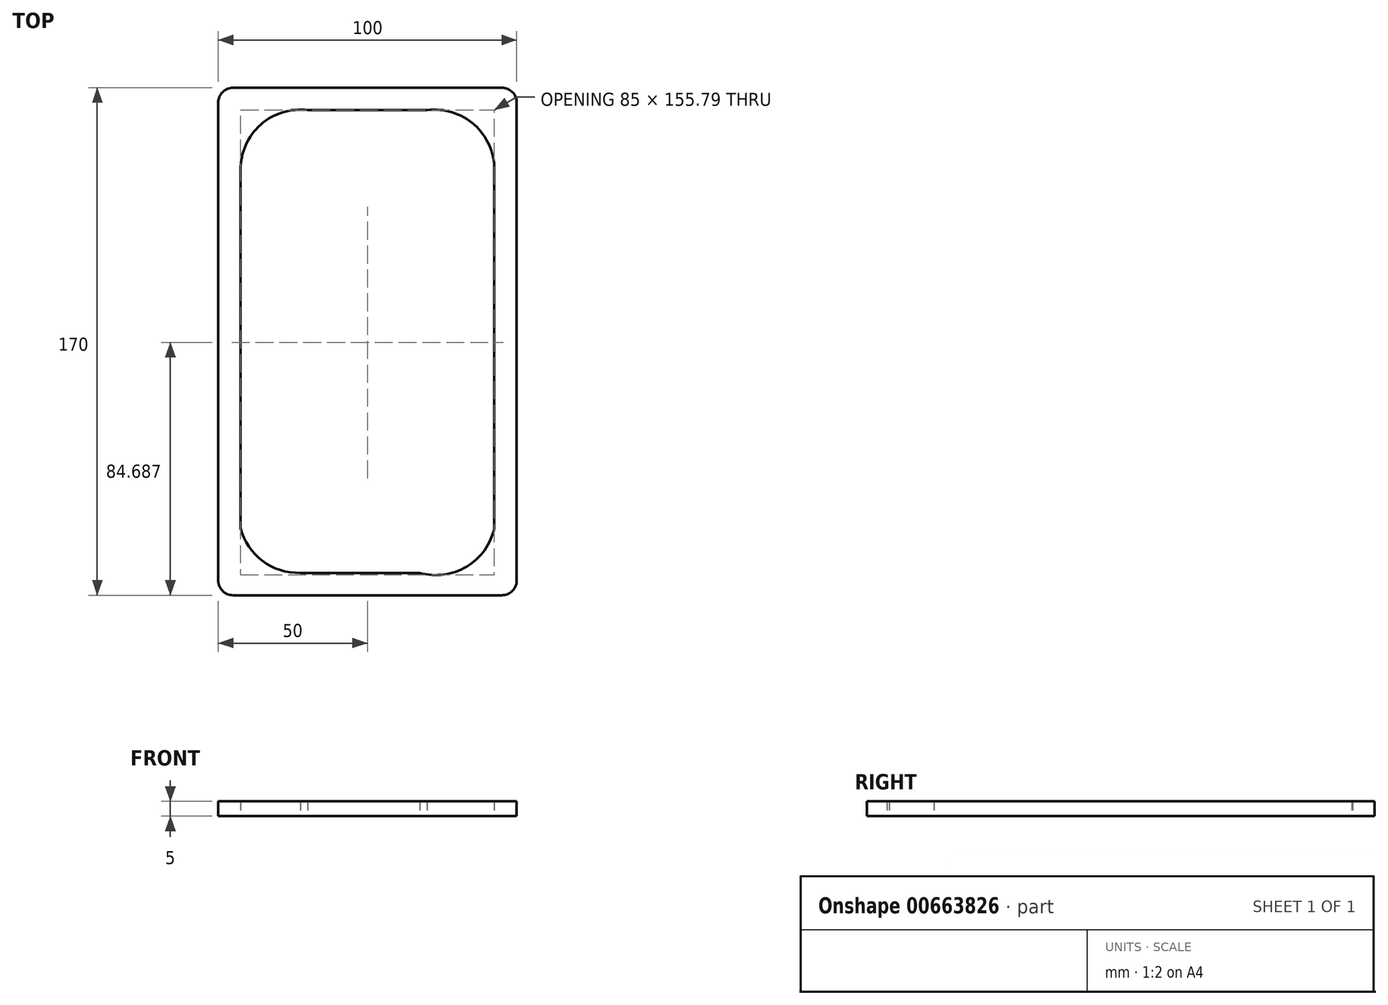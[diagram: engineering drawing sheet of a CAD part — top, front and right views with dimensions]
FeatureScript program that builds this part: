
annotation { "Feature Type Name" : "Feature", "Feature Type Description" : "" }
export const myFeature = defineFeature(function(context is Context, id is Id, definition is map)
    precondition{}
    {
        {
            var Q0;
            Q0=qCreatedBy(makeId("Top.planeOp"),FACE);
            var sketch = newSketch(context, id + "F0", { "sketchPlane" : qUnion([Q0])});
            skLineSegment(sketch, "E0.bottom", {"start": v(-45, -85) * mm, "end": v(45, -85) * mm});
            skLineSegment(sketch, "E0.top", {"start": v(-45, 85) * mm, "end": v(45, 85) * mm});
            skLineSegment(sketch, "E0.left", {"start": v(-50, -80) * mm, "end": v(-50, 80) * mm});
            skLineSegment(sketch, "E0.right", {"start": v(50, -80) * mm, "end": v(50, 80) * mm});
            skPoint(sketch, "E0.middle", {"position": v(0, 0) * mm});
            skLineSegment(sketch, "E1.bottom", {"start": v(-22.5, -77.5) * mm, "end": v(17.5, -77.5) * mm});
            skLineSegment(sketch, "E1.top", {"start": v(-20, 77.5) * mm, "end": v(20, 77.5) * mm});
            skLineSegment(sketch, "E1.left", {"start": v(-42.5, -62.5) * mm, "end": v(-42.5, 57.5) * mm});
            skLineSegment(sketch, "E1.right", {"start": v(42.5, -62.5) * mm, "end": v(42.5, 57.5) * mm});
            skPoint(sketch, "E2.visualSharp", {"position": v(-42.5, 77.5) * mm});
            skPoint(sketch, "E3.visualSharp", {"position": v(-50, 85) * mm});
            skArc(sketch, "E3.filletArc", {"start": v(-45, 85) * mm, "mid": v(-48.54, 83.54) * mm, "end": v(-50, 80) * mm});
            skPoint(sketch, "E4.visualSharp", {"position": v(50, 85) * mm});
            skArc(sketch, "E4.filletArc", {"start": v(50, 80) * mm, "mid": v(48.54, 83.54) * mm, "end": v(45, 85) * mm});
            skPoint(sketch, "E5.visualSharp", {"position": v(42.5, -77.5) * mm});
            skPoint(sketch, "E6.visualSharp", {"position": v(-42.5, -77.5) * mm});
            skPoint(sketch, "E7.visualSharp", {"position": v(-50, -85) * mm});
            skArc(sketch, "E7.filletArc", {"start": v(-50, -80) * mm, "mid": v(-48.54, -83.54) * mm, "end": v(-45, -85) * mm});
            skPoint(sketch, "E8.visualSharp", {"position": v(50, -85) * mm});
            skArc(sketch, "E8.filletArc", {"start": v(45, -85) * mm, "mid": v(48.54, -83.54) * mm, "end": v(50, -80) * mm});
            skPoint(sketch, "E9.visualSharp", {"position": v(42.5, 77.5) * mm});
            skArc(sketch, "E10", {"start": v(-42.5, 57.5) * mm, "mid": v(-35.79, 72.6) * mm, "end": v(-20, 77.5) * mm});
            skArc(sketch, "E11", {"start": v(20, 77.5) * mm, "mid": v(35.79, 72.6) * mm, "end": v(42.5, 57.5) * mm});
            skArc(sketch, "E12", {"start": v(-22.5, -77.5) * mm, "mid": v(-35.13, -73.51) * mm, "end": v(-42.5, -62.5) * mm});
            skArc(sketch, "E13", {"start": v(42.5, -62.5) * mm, "mid": v(33.24, -75.4) * mm, "end": v(17.5, -77.5) * mm});
            skSolve(sketch);
        }
        {
            var Q0;
            Q0=makeQuery(id+"F0.imprint","IMPRINT",FACE,{"disambiguationData":[TD([[makeQuery(id+"F0.imprint","IMPRINT",EDGE,{"derivedFrom":sQuery(id+"F0.wireOp",EDGE,"E0.bottom")}),1.0]])]});
            extrude(context, id + "F1", {"entities" : qUnion([Q0]), "depth" : 5 * mm, "offsetDistance" : 25 * mm});
        }
    });
